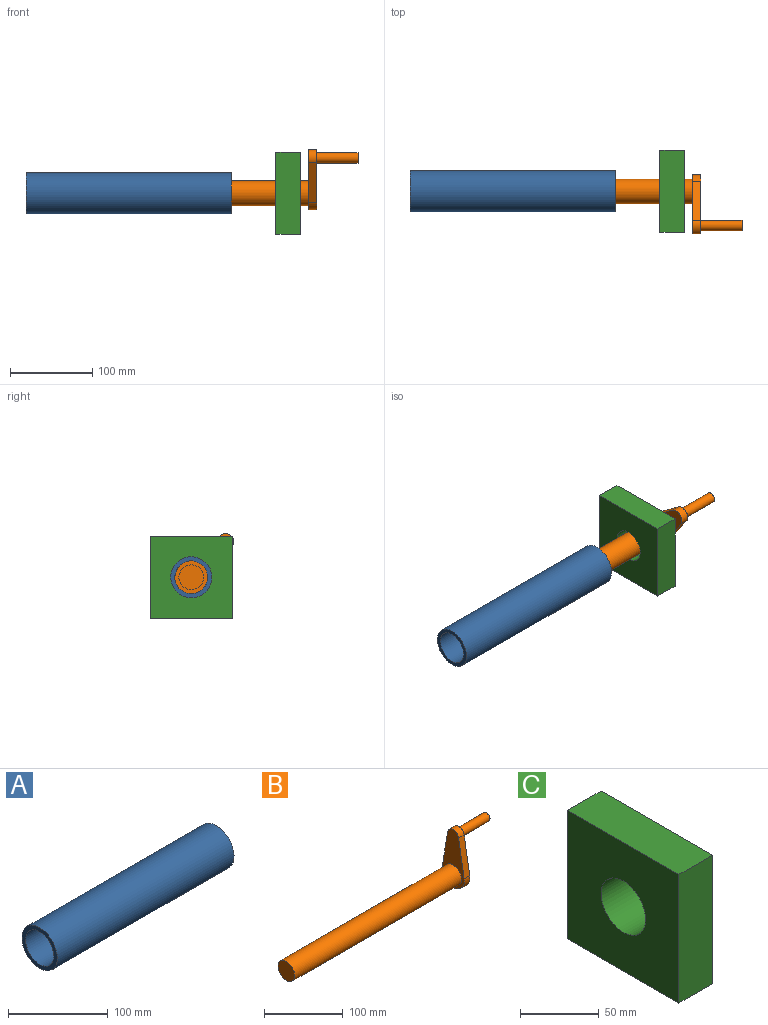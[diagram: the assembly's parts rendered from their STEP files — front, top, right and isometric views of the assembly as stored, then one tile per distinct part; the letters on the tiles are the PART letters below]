
ASSEMBLY  parts=3 mates=2
PART A: 4 faces, bbox 250x50x50 mm
  f0: cylinder r=20mm len=250mm, axis (-1,0,0), area 31415.9mm2, adj f2,f3
  f1: cylinder r=25mm len=250mm, axis (-1,0,0), area 39269.9mm2, adj f2,f3
  f2: plane 50x50mm, normal (1,0,0), area 706.9mm2, adj f0,f1
  f3: plane 50x50mm, normal (-1,0,0), area 706.9mm2, adj f0,f1
PART B: 10 faces, bbox 360x40x90 mm
  f0: cylinder r=15mm len=300mm, axis (-1,0,0), area 28274.3mm2, adj f1,f7
  f1: plane 30x30mm, normal (-1,0,0), area 706.9mm2, adj f0
  f2: cylinder r=10mm len=19.72mm, axis (-1,0,0), area 280.7mm2, adj f3,f5,f6,f7
  f3: plane 58.33x10mm, normal (0,-0.99,0.17), area 591.6mm2, adj f2,f4,f6,f7
  f4: cylinder r=20mm len=40mm, axis (-1,0,0), area 695.3mm2, adj f3,f5,f6,f7
  f5: plane 58.33x10mm, normal (0,0.99,0.17), area 591.6mm2, adj f2,f4,f6,f7
  f6: plane 90x40mm, normal (1,0,0), area 2487.7mm2, adj f2,f3,f4,f5,f8
  f7: plane 90x40mm, normal (-1,0,0), area 1903.6mm2, adj f0,f2,f3,f4,f5
  f8: cylinder r=6.25mm len=50mm, axis (-1,0,0), area 1963.5mm2, adj f6,f9
  f9: plane 12.5x12.5mm, normal (1,0,0), area 122.7mm2, adj f8
PART C: 7 faces, bbox 30x100x100 mm
  f0: plane 100x30mm, normal (0,1,0), area 3000mm2, adj f1,f3,f5,f6
  f1: plane 100x30mm, normal (0,0,1), area 3000mm2, adj f0,f2,f5,f6
  f2: plane 100x30mm, normal (0,-1,0), area 3000mm2, adj f1,f3,f5,f6
  f3: plane 100x30mm, normal (0,0,-1), area 3000mm2, adj f0,f2,f5,f6
  f4: cylinder r=20mm len=40mm, axis (-1,0,0), area 3769.9mm2, adj f5,f6
  f5: plane 100x100mm, normal (1,0,0), area 8743.4mm2, adj f0,f1,f2,f3,f4
  f6: plane 100x100mm, normal (-1,0,0), area 8743.4mm2, adj f0,f1,f2,f3,f4
PLACE A rot(axis=(-1,0,0),50.4deg) t=(-156.82,72.68,-47.68)mm
PLACE B rot(axis=(1,0,0),44.2deg) t=(-112.57,72.68,-47.68)mm
PLACE C t=(-102.57,72.68,-47.68)mm fixed
MATE cylindrical A.f1 <-> B.f0  axis (-1,0,0) through (-156.82,72.68,-47.68)mm
MATE revolute C.f4 <-> B.f0  axis (-1,0,0) through (177.43,72.68,-47.68)mm
